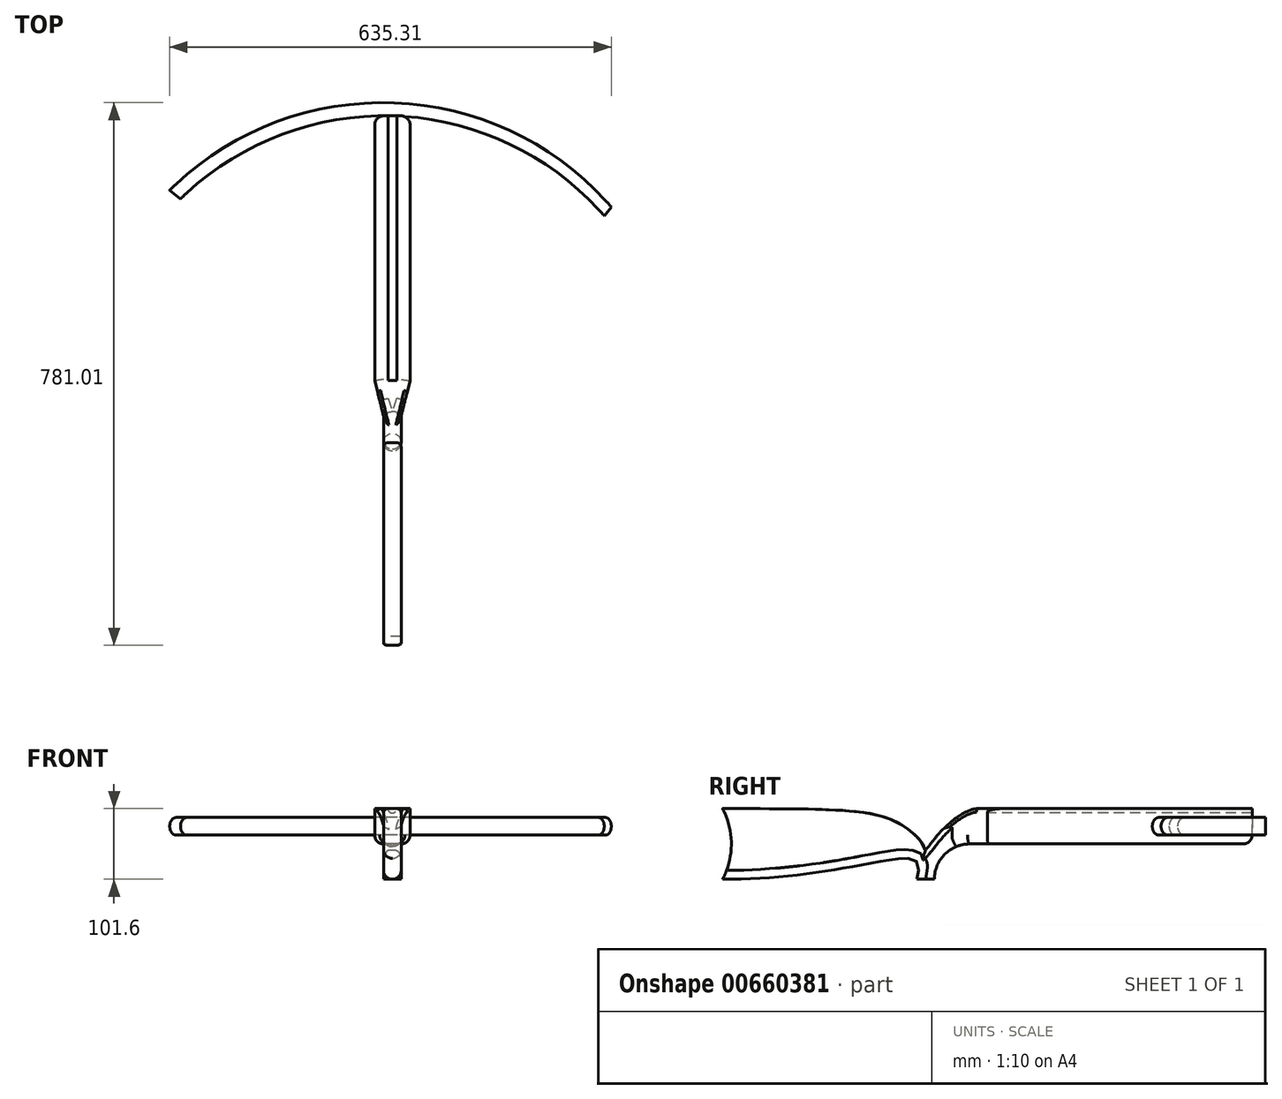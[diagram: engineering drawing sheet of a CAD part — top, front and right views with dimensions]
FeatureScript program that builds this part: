
annotation { "Feature Type Name" : "Feature", "Feature Type Description" : "" }
export const myFeature = defineFeature(function(context is Context, id is Id, definition is map)
    precondition{}
    {
        {
            var Q0;
            Q0=qCreatedBy(makeId("Right.planeOp"),FACE);
            var sketch = newSketch(context, id + "F0", { "sketchPlane" : qUnion([Q0])});
            skLineSegment(sketch, "E0.bottom", {"start": v(381, 0) * mm, "end": v(-381, 0) * mm, "construction": true});
            skLineSegment(sketch, "E0.top", {"start": v(381, 101.6) * mm, "end": v(-381, 101.6) * mm, "construction": true});
            skLineSegment(sketch, "E0.left", {"start": v(381, 50.8) * mm, "end": v(381, 101.6) * mm, "construction": true});
            skLineSegment(sketch, "E0.right", {"start": v(-381, 0) * mm, "end": v(-381, 101.6) * mm, "construction": true});
            skLineSegment(sketch, "E1", {"start": v(-76.2, 101.6) * mm, "end": v(-76.2, 0) * mm, "construction": true});
            skLineSegment(sketch, "E2", {"start": v(-101.6, 0) * mm, "end": v(-101.6, 101.6) * mm, "construction": true});
            skLineSegment(sketch, "E3.left", {"start": v(-101.6, 50.8) * mm, "end": v(-101.6, 50.8) * mm});
            skLineSegment(sketch, "E3.right", {"start": v(-381, 50.8) * mm, "end": v(-381, 50.8) * mm});
            skLineSegment(sketch, "E4", {"start": v(381, 50.8) * mm, "end": v(-76.2, 50.8) * mm, "construction": true});
            skArc(sketch, "E5", {"start": v(-381, 0) * mm, "mid": v(-368.3, 50.8) * mm, "end": v(-381, 101.6) * mm});
            skArc(sketch, "E6", {"start": v(-25.4, 50.8) * mm, "mid": v(-61.32, 35.92) * mm, "end": v(-76.2, 0) * mm});
            skFitSpline(sketch, "E7", {"points": [v(-101.6, 0) * mm, v(-101.6, 25.4) * mm, v(-381, 0) * mm], "startDerivative": vector(37.42, 107.87) * mm, "endDerivative": vector(-648.42, 0) * mm});
            skFitSpline(sketch, "E8", {"points": [v(-89.38, 41.39) * mm, v(-120.28, 76.2) * mm, v(-381, 101.6) * mm], "startDerivative": vector(-1.01, 97.2) * mm, "endDerivative": vector(-766.69, 0) * mm});
            skFitSpline(sketch, "E9", {"points": [v(-89.38, 41.39) * mm, v(-61.34, 74.32) * mm, v(-14.3, 101.6) * mm], "startDerivative": vector(44.73, 51.83) * mm, "endDerivative": vector(74.15, 0) * mm});
            skLineSegment(sketch, "E10", {"start": v(-25.4, 50.8) * mm, "end": v(368.3, 50.8) * mm});
            skLineSegment(sketch, "E11", {"start": v(381, 50.8) * mm, "end": v(381, 50.8) * mm});
            skLineSegment(sketch, "E12", {"start": v(381, 63.5) * mm, "end": v(381, 101.6) * mm});
            skLineSegment(sketch, "E13", {"start": v(381, 101.6) * mm, "end": v(-14.3, 101.6) * mm});
            skPoint(sketch, "E14.visualSharp", {"position": v(381, 50.8) * mm});
            skArc(sketch, "E14.filletArc", {"start": v(368.3, 50.8) * mm, "mid": v(377.28, 54.52) * mm, "end": v(381, 63.5) * mm});
            skLineSegment(sketch, "E15", {"start": v(-101.6, 0) * mm, "end": v(-76.2, 0) * mm});
            skSolve(sketch);
        }
        {
            var Q0;
            Q0 = qSketchRegion(id + "F0", true);
            extrude(context, id + "F1", {"entities" : qUnion([Q0]), "depth" : 25.4 * mm, "offsetDistance" : 25.4 * mm, "hasSecondDirection" : true, "secondDirectionOppositeDirection" : true, "secondDirectionDepth" : 25.4 * mm});
        }
        {
            var Q0;
            Q0=qCreatedBy(makeId("Top.planeOp"),FACE);
            var sketch = newSketch(context, id + "F2", { "sketchPlane" : qUnion([Q0])});
            skLineSegment(sketch, "E16.bottom", {"start": v(-25.4, 0) * mm, "end": v(25.4, 0) * mm, "construction": true});
            skLineSegment(sketch, "E16.top", {"start": v(-25.4, -381) * mm, "end": v(25.4, -381) * mm});
            skLineSegment(sketch, "E16.left", {"start": v(-25.4, 0) * mm, "end": v(-25.4, -381) * mm});
            skLineSegment(sketch, "E16.right", {"start": v(25.4, 0) * mm, "end": v(25.4, -381) * mm});
            skLineSegment(sketch, "E17.bottom", {"start": v(-12.7, -381) * mm, "end": v(12.7, -381) * mm});
            skLineSegment(sketch, "E17.left", {"start": v(-12.7, -381) * mm, "end": v(-12.7, -50.8) * mm});
            skLineSegment(sketch, "E17.right", {"start": v(12.7, -381) * mm, "end": v(12.7, -50.8) * mm});
            skLineSegment(sketch, "E18", {"start": v(-12.7, -50.8) * mm, "end": v(-25.4, 0) * mm});
            skLineSegment(sketch, "E19", {"start": v(12.7, -50.8) * mm, "end": v(25.4, 0) * mm});
            skSolve(sketch);
        }
        {
            var Q0;
            Q0 = qSketchRegion(id + "F2", true);
            extrude(context, id + "F3", {"entities" : qUnion([Q0]), "operationType" : NewBodyOperationType.REMOVE, "depth" : 152.4 * mm, "offsetDistance" : 25.4 * mm});
        }
        {
            var Q0;
            Q0=makeQuery(id+"F3.boolean.opBoolean","INTERSECT",EDGE,{"derivedFrom":[makeQuery(id+"F1.opExtrude","SWEPT_FACE",FACE,{"disambiguationData":[OSD([sQuery(id+"F0.wireOp",EDGE,"E6")])]}),makeQuery(id+"F3.opExtrude","SWEPT_FACE",FACE,{"disambiguationData":[OSD([sQuery(id+"F2.wireOp",EDGE,"E17.right")])]})]});
            var Q1;
            Q1=makeQuery(id+"F3.boolean.opBoolean","INTERSECT",EDGE,{"derivedFrom":[makeQuery(id+"F1.opExtrude","SWEPT_FACE",FACE,{"disambiguationData":[OSD([sQuery(id+"F0.wireOp",EDGE,"E7")])]}),makeQuery(id+"F3.opExtrude","SWEPT_FACE",FACE,{"disambiguationData":[OSD([sQuery(id+"F2.wireOp",EDGE,"E17.right")])]})]});
            var Q2;
            Q2=makeQuery(id+"F3.boolean.opBoolean","INTERSECT",EDGE,{"derivedFrom":[makeQuery(id+"F1.opExtrude","SWEPT_FACE",FACE,{"disambiguationData":[OSD([sQuery(id+"F0.wireOp",EDGE,"E7")])]}),makeQuery(id+"F3.opExtrude","SWEPT_FACE",FACE,{"disambiguationData":[OSD([sQuery(id+"F2.wireOp",EDGE,"E17.left")])]})]});
            var Q3;
            Q3=makeQuery(id+"F3.boolean.opBoolean","INTERSECT",EDGE,{"derivedFrom":[makeQuery(id+"F1.opExtrude","SWEPT_FACE",FACE,{"disambiguationData":[OSD([sQuery(id+"F0.wireOp",EDGE,"E6")])]}),makeQuery(id+"F3.opExtrude","SWEPT_FACE",FACE,{"disambiguationData":[OSD([sQuery(id+"F2.wireOp",EDGE,"E17.left")])]})]});
            var Q4;
            Q4=makeQuery(id+"F3.boolean.opBoolean","INTERSECT",EDGE,{"derivedFrom":[makeQuery(id+"F1.opExtrude","SWEPT_FACE",FACE,{"disambiguationData":[OSD([sQuery(id+"F0.wireOp",EDGE,"E6")])]}),makeQuery(id+"F3.opExtrude","SWEPT_FACE",FACE,{"disambiguationData":[OSD([sQuery(id+"F2.wireOp",EDGE,"E18")])]})]});
            var Q5;
            Q5=makeQuery(id+"F1.opExtrude","CAP_EDGE",EDGE,{"disambiguationData":[OSD([sQuery(id+"F0.wireOp",EDGE,"E10")])],"isStart":true});
            var Q6;
            Q6=makeQuery(id+"F3.boolean.opBoolean","INTERSECT",EDGE,{"derivedFrom":[makeQuery(id+"F1.opExtrude","SWEPT_FACE",FACE,{"disambiguationData":[OSD([sQuery(id+"F0.wireOp",EDGE,"E10")])]}),makeQuery(id+"F3.opExtrude","SWEPT_FACE",FACE,{"disambiguationData":[OSD([sQuery(id+"F2.wireOp",EDGE,"E18")])]})]});
            var Q7;
            Q7=makeQuery(id+"F3.boolean.opBoolean","INTERSECT",EDGE,{"derivedFrom":[makeQuery(id+"F1.opExtrude","SWEPT_FACE",FACE,{"disambiguationData":[OSD([sQuery(id+"F0.wireOp",EDGE,"E6")])]}),makeQuery(id+"F3.opExtrude","SWEPT_FACE",FACE,{"disambiguationData":[OSD([sQuery(id+"F2.wireOp",EDGE,"E19")])]})]});
            var Q8;
            Q8=makeQuery(id+"F3.boolean.opBoolean","INTERSECT",EDGE,{"derivedFrom":[makeQuery(id+"F1.opExtrude","SWEPT_FACE",FACE,{"disambiguationData":[OSD([sQuery(id+"F0.wireOp",EDGE,"E10")])]}),makeQuery(id+"F3.opExtrude","SWEPT_FACE",FACE,{"disambiguationData":[OSD([sQuery(id+"F2.wireOp",EDGE,"E19")])]})]});
            var Q9;
            Q9=makeQuery(id+"F1.opExtrude","CAP_EDGE",EDGE,{"disambiguationData":[OSD([sQuery(id+"F0.wireOp",EDGE,"E10")])],"isStart":false});
            fillet(context, id + "F4", {"entities" : qUnion([Q0, Q1, Q2, Q3, Q4, Q5, Q6, Q7, Q8, Q9]), "radius" : 12.7 * mm, "tangentPropagation" : true, "allowEdgeOverflow" : false});
        }
        {
            var Q0;
            Q0=makeQuery(id+"F3.boolean.opBoolean","INTERSECT",EDGE,{"derivedFrom":[makeQuery(id+"F1.opExtrude","SWEPT_FACE",FACE,{"disambiguationData":[OSD([sQuery(id+"F0.wireOp",EDGE,"E8")])]}),makeQuery(id+"F3.opExtrude","SWEPT_FACE",FACE,{"disambiguationData":[OSD([sQuery(id+"F2.wireOp",EDGE,"E17.left")])]})]});
            var Q1;
            Q1=makeQuery(id+"F3.boolean.opBoolean","INTERSECT",EDGE,{"derivedFrom":[makeQuery(id+"F1.opExtrude","SWEPT_FACE",FACE,{"disambiguationData":[OSD([sQuery(id+"F0.wireOp",EDGE,"E8")])]}),makeQuery(id+"F3.opExtrude","SWEPT_FACE",FACE,{"disambiguationData":[OSD([sQuery(id+"F2.wireOp",EDGE,"E17.right")])]})]});
            fillet(context, id + "F5", {"entities" : qUnion([Q0, Q1]), "radius" : 6.35 * mm, "tangentPropagation" : true, "allowEdgeOverflow" : false});
        }
        {
            var Q0;
            Q0=makeQuery(id+"F3.boolean.opBoolean","INTERSECT",EDGE,{"derivedFrom":[makeQuery(id+"F1.opExtrude","SWEPT_FACE",FACE,{"disambiguationData":[OSD([sQuery(id+"F0.wireOp",EDGE,"E9")])]}),makeQuery(id+"F3.opExtrude","SWEPT_FACE",FACE,{"disambiguationData":[OSD([sQuery(id+"F2.wireOp",EDGE,"E17.left")])]})]});
            var Q1;
            Q1=makeQuery(id+"F3.boolean.opBoolean","INTERSECT",EDGE,{"derivedFrom":[makeQuery(id+"F1.opExtrude","SWEPT_FACE",FACE,{"disambiguationData":[OSD([sQuery(id+"F0.wireOp",EDGE,"E9")])]}),makeQuery(id+"F3.opExtrude","SWEPT_FACE",FACE,{"disambiguationData":[OSD([sQuery(id+"F2.wireOp",EDGE,"E17.right")])]})]});
            fillet(context, id + "F6", {"entities" : qUnion([Q0, Q1]), "radius" : 7.62 * mm, "tangentPropagation" : true, "allowEdgeOverflow" : false});
        }
        {
            var Q0;
            Q0=makeQuery(id+"F3.boolean.opBoolean","INTERSECT",EDGE,{"derivedFrom":[makeQuery(id+"F1.opExtrude","SWEPT_FACE",FACE,{"disambiguationData":[OSD([sQuery(id+"F0.wireOp",EDGE,"E9")])]}),makeQuery(id+"F3.opExtrude","SWEPT_FACE",FACE,{"disambiguationData":[OSD([sQuery(id+"F2.wireOp",EDGE,"E18")])]})]});
            var Q1;
            Q1=makeQuery(id+"F3.boolean.opBoolean","INTERSECT",EDGE,{"derivedFrom":[makeQuery(id+"F1.opExtrude","SWEPT_FACE",FACE,{"disambiguationData":[OSD([sQuery(id+"F0.wireOp",EDGE,"E9")])]}),makeQuery(id+"F3.opExtrude","SWEPT_FACE",FACE,{"disambiguationData":[OSD([sQuery(id+"F2.wireOp",EDGE,"E19")])]})]});
            fillet(context, id + "F7", {"entities" : qUnion([Q0, Q1]), "radius" : 5.08 * mm, "tangentPropagation" : true, "allowEdgeOverflow" : false});
        }
        {
            var Q0;
            Q0=qCreatedBy(makeId("Top.planeOp"),FACE);
            var sketch = newSketch(context, id + "F8", { "sketchPlane" : qUnion([Q0])});
            skLineSegment(sketch, "E20.bottom", {"start": v(-25.4, 0) * mm, "end": v(25.4, 0) * mm, "construction": true});
            skLineSegment(sketch, "E20.top", {"start": v(-25.4, 381) * mm, "end": v(25.4, 381) * mm, "construction": true});
            skLineSegment(sketch, "E20.left", {"start": v(-25.4, 0) * mm, "end": v(-25.4, 381) * mm, "construction": true});
            skLineSegment(sketch, "E20.right", {"start": v(25.4, 0) * mm, "end": v(25.4, 381) * mm, "construction": true});
            skLineSegment(sketch, "E21.bottom", {"start": v(-6.35, 381) * mm, "end": v(6.35, 381) * mm});
            skLineSegment(sketch, "E21.top", {"start": v(-6.35, 0) * mm, "end": v(6.35, 0) * mm});
            skLineSegment(sketch, "E21.left", {"start": v(-6.35, 381) * mm, "end": v(-6.35, 0) * mm});
            skLineSegment(sketch, "E21.right", {"start": v(6.35, 381) * mm, "end": v(6.35, 0) * mm});
            skSolve(sketch);
        }
        {
            var Q0;
            Q0 = qSketchRegion(id + "F8", true);
            extrude(context, id + "F9", {"entities" : qUnion([Q0]), "operationType" : NewBodyOperationType.REMOVE, "depth" : 152.4 * mm, "offsetDistance" : 25.4 * mm, "hasSecondDirection" : true, "secondDirectionOppositeDirection" : false, "secondDirectionDepth" : 95.25 * mm});
        }
        {
            var Q0;
            Q0=makeQuery(id+"F9.boolean.opBoolean","COPY",EDGE,{"derivedFrom":makeQuery(id+"F9.opExtrude","CAP_EDGE",EDGE,{"disambiguationData":[OSD([sQuery(id+"F8.wireOp",EDGE,"E21.right")])],"isStart":true})});
            var Q1;
            Q1=makeQuery(id+"F9.boolean.opBoolean","COPY",EDGE,{"derivedFrom":makeQuery(id+"F9.opExtrude","CAP_EDGE",EDGE,{"disambiguationData":[OSD([sQuery(id+"F8.wireOp",EDGE,"E21.left")])],"isStart":true})});
            fillet(context, id + "F10", {"entities" : qUnion([Q0, Q1]), "radius" : 6.35 * mm, "tangentPropagation" : true, "allowEdgeOverflow" : false});
        }
        {
            var Q0;
            Q0=qCreatedBy(makeId("Top.planeOp"),FACE);
            var sketch = newSketch(context, id + "F11", { "sketchPlane" : qUnion([Q0])});
            skPoint(sketch, "E22", {"position": v(0, 381) * mm});
            skArc(sketch, "E23", {"start": v(304.8, 237.25) * mm, "mid": v(5.22, 380.83) * mm, "end": v(-304.8, 261.43) * mm});
            skArc(sketch, "E24", {"start": v(315.05, 249.95) * mm, "mid": v(2.63, 399.7) * mm, "end": v(-320.26, 274.13) * mm});
            skLineSegment(sketch, "E25", {"start": v(315.05, 249.95) * mm, "end": v(304.8, 237.25) * mm});
            skLineSegment(sketch, "E26", {"start": v(-320.26, 274.13) * mm, "end": v(-304.8, 261.43) * mm});
            skSolve(sketch);
        }
        {
            var Q0;
            Q0 = qSketchRegion(id + "F11", true);
            extrude(context, id + "F12", {"entities" : qUnion([Q0]), "depth" : 88.9 * mm, "offsetDistance" : 25.4 * mm, "hasSecondDirection" : true, "secondDirectionOppositeDirection" : false, "secondDirectionDepth" : 63.5 * mm});
        }
        {
            var Q0;
            Q0=makeQuery(id+"F12.opExtrude","CAP_EDGE",EDGE,{"disambiguationData":[OSD([sQuery(id+"F11.wireOp",EDGE,"E26")])],"isStart":false});
            var Q1;
            Q1=makeQuery(id+"F12.opExtrude","CAP_EDGE",EDGE,{"disambiguationData":[OSD([sQuery(id+"F11.wireOp",EDGE,"E26")])],"isStart":true});
            var Q2;
            Q2=makeQuery(id+"F12.opExtrude","CAP_EDGE",EDGE,{"disambiguationData":[OSD([sQuery(id+"F11.wireOp",EDGE,"E25")])],"isStart":false});
            var Q3;
            Q3=makeQuery(id+"F12.opExtrude","CAP_EDGE",EDGE,{"disambiguationData":[OSD([sQuery(id+"F11.wireOp",EDGE,"E25")])],"isStart":true});
            fillet(context, id + "F13", {"entities" : qUnion([Q0, Q1, Q2, Q3]), "radius" : 12.7 * mm, "tangentPropagation" : true, "allowEdgeOverflow" : false});
        }
    });
